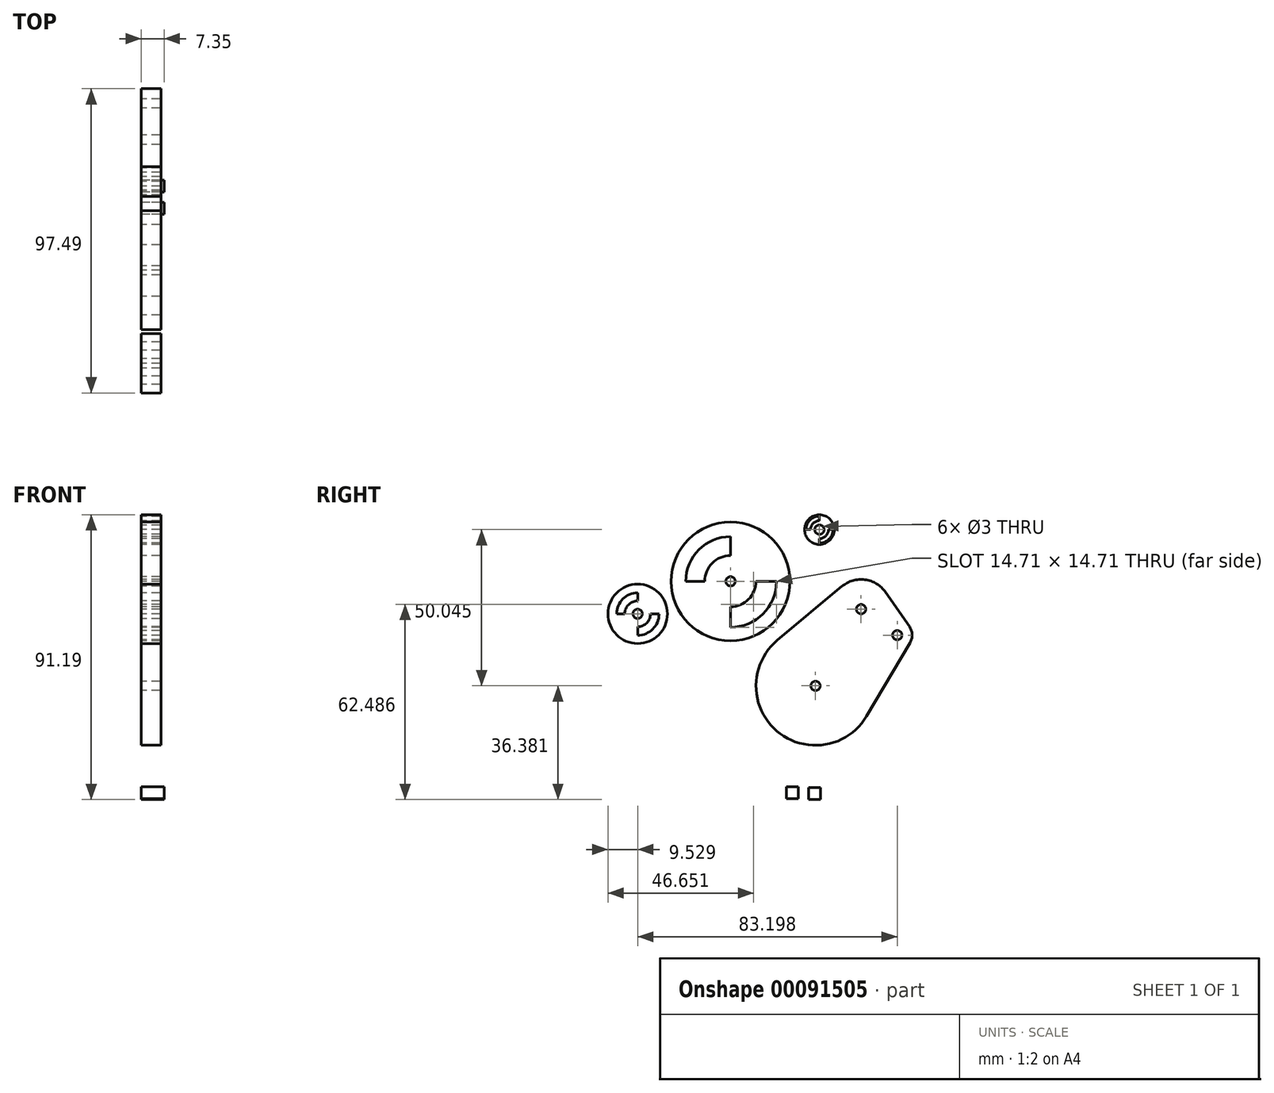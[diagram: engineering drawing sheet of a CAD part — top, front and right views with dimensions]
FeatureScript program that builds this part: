
annotation { "Feature Type Name" : "Feature", "Feature Type Description" : "" }
export const myFeature = defineFeature(function(context is Context, id is Id, definition is map)
    precondition{}
    {
        {
            var Q0;
            Q0=qCreatedBy(makeId("Right.planeOp"),FACE);
            var sketch = newSketch(context, id + "F0", { "sketchPlane" : qUnion([Q0])});
            skArc(sketch, "E0", {"start": v(-7.06, 29.74) * mm, "mid": v(-6.4, 32.34) * mm, "end": v(-7.25, 34.9) * mm});
            skArc(sketch, "E1", {"start": v(-49.56, 30.58) * mm, "mid": v(-49.72, 1.44) * mm, "end": v(-20.98, 6.23) * mm});
            skArc(sketch, "E2", {"start": v(-14.94, 45.94) * mm, "mid": v(-21.49, 49.94) * mm, "end": v(-28.86, 47.82) * mm});
            skCircle(sketch, "E3", {"center": v(-94.35, 39) * mm, "radius": 9.53 * mm});
            skCircle(sketch, "E4", {"center": v(-64.59, 49.4) * mm, "radius": 19.05 * mm});
            skCircle(sketch, "E5", {"center": v(-36.1, 65.99) * mm, "radius": 4.76 * mm});
            skLineSegment(sketch, "E6", {"start": v(-14.94, 45.94) * mm, "end": v(-7.25, 34.9) * mm});
            skLineSegment(sketch, "E7", {"start": v(-20.98, 6.23) * mm, "end": v(-7.06, 29.74) * mm});
            skLineSegment(sketch, "E8", {"start": v(-49.56, 30.58) * mm, "end": v(-28.86, 47.82) * mm});
            skPoint(sketch, "E9.orphan", {"position": v(0, 71.85) * mm});
            skCircle(sketch, "E10", {"center": v(-64.59, 49.4) * mm, "radius": 1.5 * mm});
            skCircle(sketch, "E11", {"center": v(-36.1, 65.99) * mm, "radius": 1.5 * mm});
            skCircle(sketch, "E12", {"center": v(-94.35, 39) * mm, "radius": 1.5 * mm});
            skCircle(sketch, "E13", {"center": v(-37.37, 15.94) * mm, "radius": 1.5 * mm});
            skCircle(sketch, "E14", {"center": v(-22.76, 40.5) * mm, "radius": 1.5 * mm});
            skCircle(sketch, "E15", {"center": v(-11.15, 32.17) * mm, "radius": 1.5 * mm});
            skPoint(sketch, "E16", {"position": v(-32.2, 38.2) * mm});
            skPoint(sketch, "E17", {"position": v(-15.89, 21.9) * mm});
            skArc(sketch, "E18", {"start": v(-64.59, 41.26) * mm, "mid": v(-58.83, 43.64) * mm, "end": v(-56.44, 49.4) * mm});
            skArc(sketch, "E19", {"start": v(-64.59, 34.69) * mm, "mid": v(-54.18, 39) * mm, "end": v(-49.87, 49.4) * mm});
            skLineSegment(sketch, "E20", {"start": v(-56.44, 49.4) * mm, "end": v(-49.87, 49.4) * mm});
            skLineSegment(sketch, "E21", {"start": v(-64.59, 41.26) * mm, "end": v(-64.59, 34.69) * mm});
            skArc(sketch, "E22", {"start": v(-72.88, 49.4) * mm, "mid": v(-70.45, 55.27) * mm, "end": v(-64.59, 57.7) * mm});
            skArc(sketch, "E23", {"start": v(-78.93, 49.4) * mm, "mid": v(-74.73, 59.54) * mm, "end": v(-64.59, 63.74) * mm});
            skLineSegment(sketch, "E24", {"start": v(-64.59, 63.74) * mm, "end": v(-64.59, 57.7) * mm});
            skLineSegment(sketch, "E25", {"start": v(-72.88, 49.4) * mm, "end": v(-78.93, 49.4) * mm});
            skArc(sketch, "E26", {"start": v(-94.35, 32.13) * mm, "mid": v(-89.49, 34.15) * mm, "end": v(-87.47, 39) * mm});
            skArc(sketch, "E27", {"start": v(-94.35, 34.89) * mm, "mid": v(-91.44, 36.1) * mm, "end": v(-90.23, 39) * mm});
            skArc(sketch, "E28", {"start": v(-101.06, 39) * mm, "mid": v(-99.1, 43.76) * mm, "end": v(-94.35, 45.72) * mm});
            skArc(sketch, "E29", {"start": v(-98.5, 39) * mm, "mid": v(-97.29, 41.95) * mm, "end": v(-94.35, 43.16) * mm});
            skLineSegment(sketch, "E30", {"start": v(-94.35, 45.72) * mm, "end": v(-94.35, 43.16) * mm});
            skLineSegment(sketch, "E31", {"start": v(-101.06, 39) * mm, "end": v(-98.5, 39) * mm});
            skLineSegment(sketch, "E32", {"start": v(-90.23, 39) * mm, "end": v(-87.47, 39) * mm});
            skLineSegment(sketch, "E33", {"start": v(-94.35, 34.89) * mm, "end": v(-94.35, 32.13) * mm});
            skArc(sketch, "E34", {"start": v(-36.1, 63.1) * mm, "mid": v(-34.06, 63.94) * mm, "end": v(-33.21, 65.99) * mm});
            skArc(sketch, "E35", {"start": v(-38.96, 65.99) * mm, "mid": v(-38.13, 68) * mm, "end": v(-36.1, 68.85) * mm});
            skArc(sketch, "E36", {"start": v(-36.1, 61.66) * mm, "mid": v(-33.05, 62.93) * mm, "end": v(-31.78, 65.99) * mm});
            skArc(sketch, "E37", {"start": v(-40.4, 65.99) * mm, "mid": v(-39.14, 69.02) * mm, "end": v(-36.1, 70.27) * mm});
            skLineSegment(sketch, "E38", {"start": v(-36.1, 70.27) * mm, "end": v(-36.1, 68.85) * mm});
            skLineSegment(sketch, "E39", {"start": v(-40.4, 65.99) * mm, "end": v(-38.96, 65.99) * mm});
            skLineSegment(sketch, "E40", {"start": v(-36.1, 63.1) * mm, "end": v(-36.1, 61.66) * mm});
            skLineSegment(sketch, "E41", {"start": v(-33.21, 65.99) * mm, "end": v(-31.78, 65.99) * mm});
            skSolve(sketch);
        }
        {
            var Q0;
            Q0 = qSketchRegion(id + "F0", true);
            extrude(context, id + "F1", {"entities" : qUnion([Q0]), "depth" : 6.35 * mm});
        }
        {
            var Q0;
            Q0=qCreatedBy(makeId("Right.planeOp"),FACE);
            var sketch = newSketch(context, id + "F2", { "sketchPlane" : qUnion([Q0])});
            skLineSegment(sketch, "E42.bottom", {"start": v(-46.67, -16.4) * mm, "end": v(-42.86, -16.4) * mm});
            skLineSegment(sketch, "E42.top", {"start": v(-46.67, -20.2) * mm, "end": v(-42.86, -20.2) * mm});
            skLineSegment(sketch, "E42.left", {"start": v(-46.67, -16.4) * mm, "end": v(-46.67, -20.2) * mm});
            skLineSegment(sketch, "E42.right", {"start": v(-42.86, -16.4) * mm, "end": v(-42.86, -20.2) * mm});
            skLineSegment(sketch, "E43.bottom", {"start": v(-39.57, -16.63) * mm, "end": v(-35.76, -16.63) * mm});
            skLineSegment(sketch, "E43.top", {"start": v(-39.57, -20.44) * mm, "end": v(-35.76, -20.44) * mm});
            skLineSegment(sketch, "E43.left", {"start": v(-39.57, -16.63) * mm, "end": v(-39.57, -20.44) * mm});
            skLineSegment(sketch, "E43.right", {"start": v(-35.76, -16.63) * mm, "end": v(-35.76, -20.44) * mm});
            skSolve(sketch);
        }
        {
            var Q0;
            Q0 = qSketchRegion(id + "F2", true);
            extrude(context, id + "F3", {"entities" : qUnion([Q0]), "depth" : 7.35 * mm});
        }
    });
